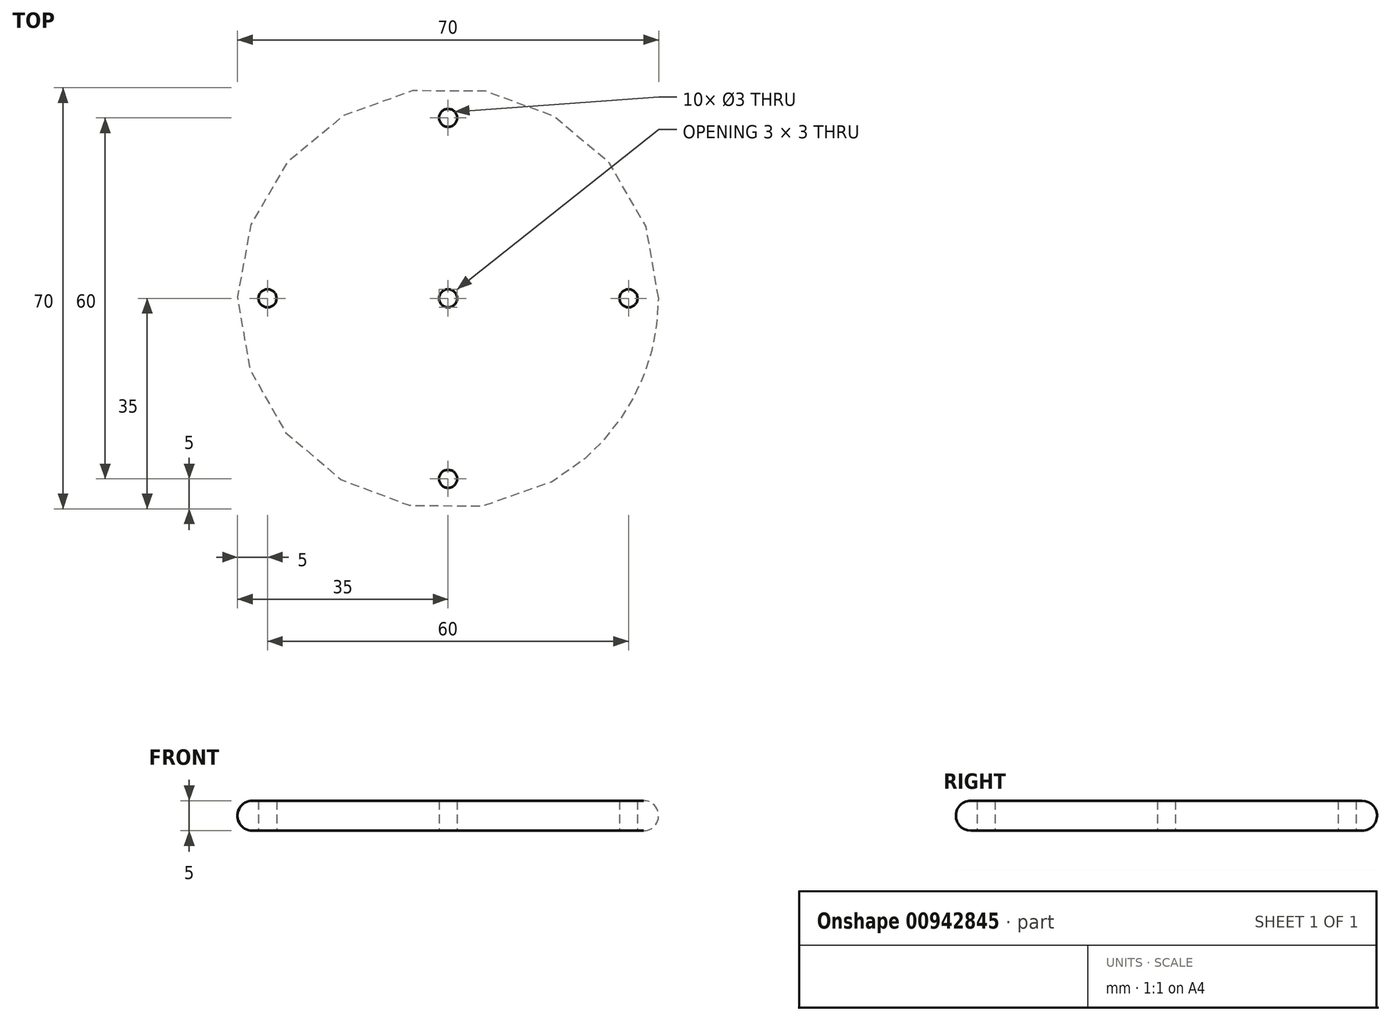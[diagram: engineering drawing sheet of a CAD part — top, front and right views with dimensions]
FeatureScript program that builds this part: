
annotation { "Feature Type Name" : "Feature", "Feature Type Description" : "" }
export const myFeature = defineFeature(function(context is Context, id is Id, definition is map)
    precondition{}
    {
        {
            var Q0;
            Q0=qCreatedBy(makeId("Top.planeOp"),FACE);
            var sketch = newSketch(context, id + "F0", { "sketchPlane" : qUnion([Q0])});
            skCircle(sketch, "E0", {"center": v(0, 0) * mm, "radius": 35 * mm});
            skCircle(sketch, "E1", {"center": v(0, 30) * mm, "radius": 1.5 * mm});
            skCircle(sketch, "E2", {"center": v(-30, 0) * mm, "radius": 1.5 * mm});
            skCircle(sketch, "E3", {"center": v(0, -30) * mm, "radius": 1.5 * mm});
            skCircle(sketch, "E4", {"center": v(30, 0) * mm, "radius": 1.5 * mm});
            skSolve(sketch);
        }
        {
            var Q0;
            Q0=makeQuery(id+"F0.imprint","IMPRINT",FACE,{"disambiguationData":[TD([[makeQuery(id+"F0.imprint","IMPRINT",EDGE,{"derivedFrom":sQuery(id+"F0.wireOp",EDGE,"E0")}),1.0]])]});
            extrude(context, id + "F1", {"entities" : qUnion([Q0]), "depth" : 5 * mm, "offsetDistance" : 25 * mm});
        }
        {
            var Q0;
            Q0=makeQuery(id+"F1.opExtrude","CAP_EDGE",EDGE,{"disambiguationData":[OSD([sQuery(id+"F0.wireOp",EDGE,"E0")])],"isStart":false});
            var Q1;
            Q1=makeQuery(id+"F1.opExtrude","CAP_EDGE",EDGE,{"disambiguationData":[OSD([sQuery(id+"F0.wireOp",EDGE,"E0")])],"isStart":true});
            fillet(context, id + "F2", {"entities" : qUnion([Q0, Q1]), "radius" : 2.5 * mm, "tangentPropagation" : true, "allowEdgeOverflow" : false});
        }
        {
            var Q0;
            Q0=sQuery(id+"F0.wireOp",VERTEX,"E0.center");
            var Q1;
            Q1=makeQuery(id+"F1.opExtrude","SWEPT_BODY",BODY,{"disambiguationData":[OSD([sQuery(id+"F0.wireOp",EDGE,"E0"),sQuery(id+"F0.wireOp",EDGE,"E1"),sQuery(id+"F0.wireOp",EDGE,"E2"),sQuery(id+"F0.wireOp",EDGE,"E3"),sQuery(id+"F0.wireOp",EDGE,"E4")])]});
            hole(context, id + "F3", {"style" : HoleStyle.SIMPLE, "endStyle" : HoleEndStyle.THROUGH, "oppositeDirection" : true, "holeDiameter" : 3 * mm, "majorDiameter" : 5 * mm, "isTappedThrough" : true, "tappedDepth" : 12 * mm, "tapClearance" : 3, "locations" : qUnion([Q0]), "scope" : qUnion([Q1])});
        }
    });
